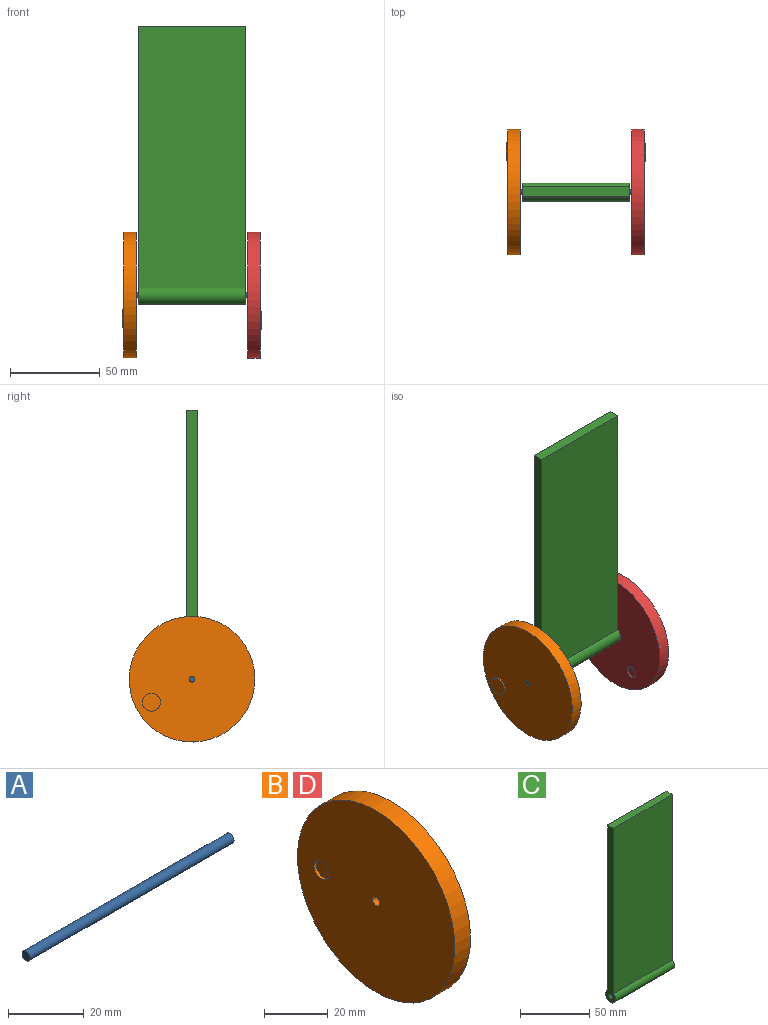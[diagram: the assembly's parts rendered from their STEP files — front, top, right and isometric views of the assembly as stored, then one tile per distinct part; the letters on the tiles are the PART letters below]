
ASSEMBLY  parts=4 mates=3
PART A: 3 faces, bbox 76x3x3 mm
  f0: cylinder r=1.5mm len=76mm, axis (-1,0,0), area 716.3mm2, adj f1,f2
  f1: plane 3x3mm, normal (1,0,0), area 7.1mm2, adj f0
  f2: plane 3x3mm, normal (-1,0,0), area 7.1mm2, adj f0
PART B: 8 faces, bbox 8x70x70 mm
  f0: cylinder r=35mm len=70mm, axis (-1,0,0), area 1539.4mm2, adj f2,f3
  f1: cylinder r=1.6mm len=7mm, axis (-1,0,0), area 70.4mm2, adj f2,f3
  f2: plane 70x70mm, normal (1,0,0), area 3761.9mm2, adj f0,f1,f4
  f3: plane 70x70mm, normal (-1,0,0), area 3804.2mm2, adj f0,f1,f6
  f4: cylinder r=5mm len=10mm, axis (-1,0,0), area 31.4mm2, adj f2,f5
  f5: plane 10x10mm, normal (1,0,0), area 78.5mm2, adj f4
  f6: cylinder r=3.4mm len=6.79mm, axis (-1,0,0), area 21.3mm2, adj f3,f7
  f7: plane 6.79x6.79mm, normal (-1,0,0), area 36.2mm2, adj f6
PART C: 7 faces, bbox 60x10x155 mm
  f0: plane 155x10mm, normal (1,0,0), area 940.8mm2, adj f1,f3,f4,f5,f6
  f1: plane 60x6mm, normal (0,0,1), area 360mm2, adj f0,f2,f3,f4
  f2: plane 155x10mm, normal (-1,0,0), area 940.8mm2, adj f1,f3,f4,f5,f6
  f3: plane 146x60mm, normal (0,-1,0), area 8760mm2, adj f0,f1,f2,f5
  f4: plane 146x60mm, normal (0,1,0), area 8760mm2, adj f0,f1,f2,f5
  f5: cylinder r=5mm len=60mm, axis (1,0,0), area 1498.9mm2, adj f0,f2,f3,f4
  f6: cylinder r=1.75mm len=60mm, axis (1,0,0), area 659.7mm2, adj f0,f2
PART D: same geometry as B
PLACE A rot(axis=(-1,0,0),121.3deg) t=(-50.36,-19.45,-60.56)mm
PLACE B rot(axis=(0,-0.87,-0.49),180deg) t=(-81.36,-12.45,-190.69)mm
PLACE C t=(-50.36,-19.45,14.44)mm fixed
PLACE D rot(axis=(-1,0,0),121.3deg) t=(-19.36,99.21,-6.71)mm
MATE revolute C.f5 <-> A.f0  axis (1,0,0) through (-20.36,-19.45,-60.56)mm
MATE fastened A.f0 <-> D.f0  axis (-1,0,0) through (-12.36,-19.45,-60.56)mm
MATE fastened A.f0 <-> B.f0  axis (-1,0,0) through (-88.36,-19.45,-60.56)mm
